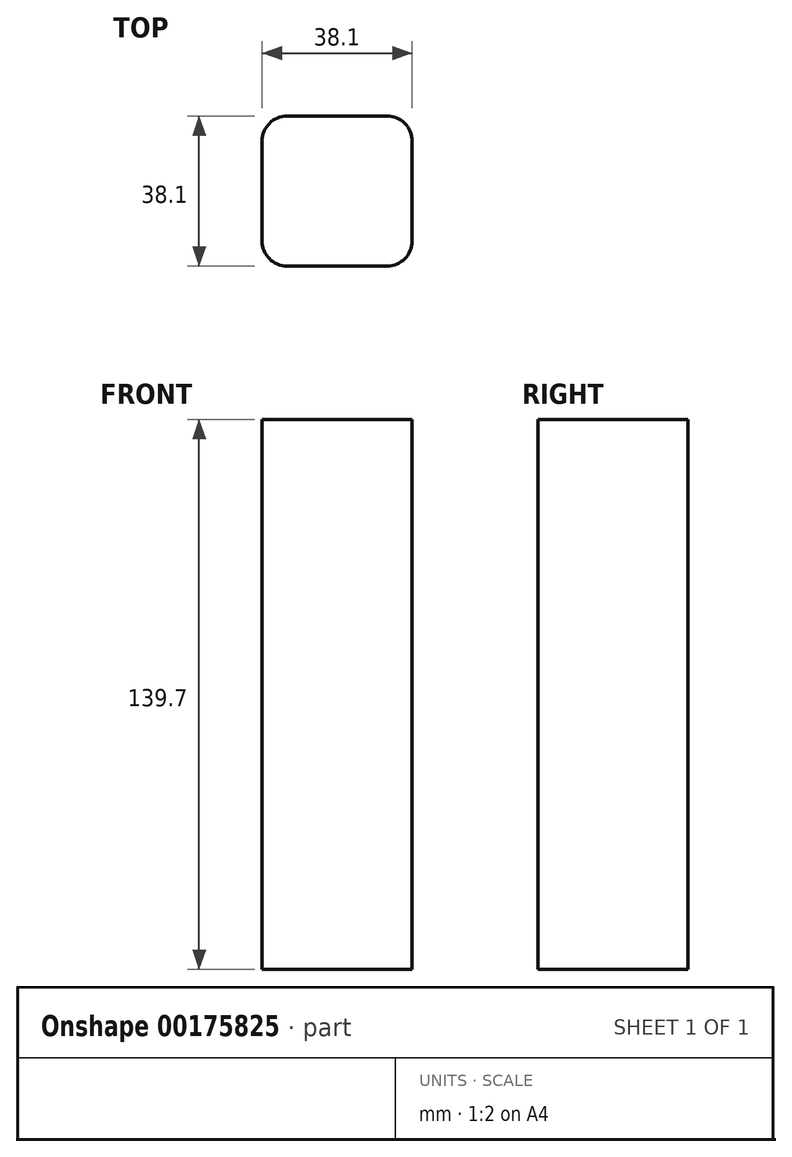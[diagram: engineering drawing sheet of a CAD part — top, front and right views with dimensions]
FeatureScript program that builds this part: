
annotation { "Feature Type Name" : "Feature", "Feature Type Description" : "" }
export const myFeature = defineFeature(function(context is Context, id is Id, definition is map)
    precondition{}
    {
        {
            var Q0;
            Q0=qCreatedBy(makeId("Top.planeOp"),FACE);
            var sketch = newSketch(context, id + "F0", { "sketchPlane" : qUnion([Q0])});
            skLineSegment(sketch, "E0.bottom", {"start": v(12.7, 19.05) * mm, "end": v(-12.7, 19.05) * mm});
            skLineSegment(sketch, "E0.top", {"start": v(12.7, -19.05) * mm, "end": v(-12.7, -19.05) * mm});
            skLineSegment(sketch, "E0.left", {"start": v(19.05, 12.7) * mm, "end": v(19.05, -12.7) * mm});
            skLineSegment(sketch, "E0.right", {"start": v(-19.05, 12.7) * mm, "end": v(-19.05, -12.7) * mm});
            skPoint(sketch, "E0.middle", {"position": v(0, 0) * mm});
            skPoint(sketch, "E1.visualSharp", {"position": v(-19.05, 19.05) * mm});
            skArc(sketch, "E1.filletArc", {"start": v(-12.7, 19.05) * mm, "mid": v(-17.2, 17.2) * mm, "end": v(-19.05, 12.7) * mm});
            skPoint(sketch, "E2.visualSharp", {"position": v(19.05, 19.05) * mm});
            skArc(sketch, "E2.filletArc", {"start": v(19.05, 12.7) * mm, "mid": v(17.2, 17.2) * mm, "end": v(12.7, 19.05) * mm});
            skPoint(sketch, "E3.visualSharp", {"position": v(19.05, -19.05) * mm});
            skArc(sketch, "E3.filletArc", {"start": v(12.7, -19.05) * mm, "mid": v(17.2, -17.2) * mm, "end": v(19.05, -12.7) * mm});
            skPoint(sketch, "E4.visualSharp", {"position": v(-19.05, -19.05) * mm});
            skArc(sketch, "E4.filletArc", {"start": v(-19.05, -12.7) * mm, "mid": v(-17.2, -17.2) * mm, "end": v(-12.7, -19.05) * mm});
            skSolve(sketch);
        }
        {
            var Q0;
            Q0=qSketchRegion(id+"F0",true);
            extrude(context, id + "F1", {"entities" : qUnion([Q0]), "depth" : 139.7 * mm, "offsetDistance" : 25.4 * mm});
        }
    });
